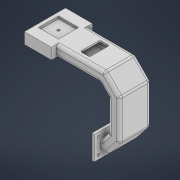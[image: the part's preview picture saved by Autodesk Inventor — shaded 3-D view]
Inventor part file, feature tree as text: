
AUTODESK INVENTOR PART (.ipt)
format: ipt  version: 2021 (Build 250183000, 183)  size: 386,560 bytes
history: native  units: mm
features: sketch x12, fillet x11, extrude x10, sweep x1, shell x1
ambient origin geometry x8: Origin, YZ Plane, XZ Plane, XY Plane, X Axis, Y Axis, Z Axis, Center Point
bodies: Volumenkörper1 (feature_tree)
feature tree (35):
  extrude  "Extrusion1"  Depth=34.2mm
  sweep  "Sweeping1"
  fillet  "Rundung1"  Radius=14.0mm
  fillet  "Rundung2"  Radius=55.9mm
  fillet  "Rundung3"  Radius=90.0mm
  fillet  "Rundung4"  Radius=45.0mm
  fillet  "Rundung5"  Radius=5.0mm
  fillet  "Rundung6"  Radius=58.0mm
  fillet  "Rundung7"  Radius=15.0mm
  fillet  "Rundung8"  [1 undecoded]
  fillet  "Rundung9"  Radius=4.0mm
  shell  "Wandung1"  Thickness=4.0mm
  extrude  "Extrusion2"  Depth=4.0mm
  extrude  "Extrusion3"  Depth=4.0mm
  fillet  "Rundung10"  Radius=4.0mm
  extrude  "Extrusion4"  Depth=4.0mm
  sketch  "Skizze13"  dims[d38=10.0mm d39=0.0mm d40=30.0mm]
  extrude  "Extrusion16"  Depth=2.0mm
  extrude  "Extrusion17"  Depth=10.0mm
  extrude  "Extrusion18"  Depth=2.0mm
  extrude  "Extrusion19"  Depth=2.0mm
  extrude  "Extrusion20"  Depth=5.0mm
  fillet  "Rundung11"  Radius=5.0mm
  extrude  "Extrusion21"  Depth=5.0mm
  sketch  "Skizze1"  dims[d0=52.0mm d1=34.2mm]
  sketch  "Skizze2"  dims[d2=14.0mm d3=0.0mm d4=40.0mm d5=14.0mm d17=55.9mm d18=90.0mm d20=45.0mm d21=5.0mm d22=58.0mm d23=15.0mm d25=0.0mm d26=0.0mm d27=4.0mm d28=4.0mm]
  sketch  "Skizze3"  dims[d29=4.0mm d30=4.0mm]
  sketch  "Skizze4"  dims[d31=4.0mm d32=4.0mm d33=4.0mm]
  sketch  "Skizze5"  dims[d34=4.0mm d35=4.0mm]
  sketch  "Skizze6"  dims[d36=2.0mm d37=2.0mm]
  sketch  "Skizze18"  dims[d41=55.0mm d42=2.0mm]
  sketch  "Skizze20"  dims[d43=3.0mm d44=0.0mm d45=2.0mm]
  sketch  "Skizze21"  dims[d46=3.2mm d47=5.0mm d48=5.0mm]
  sketch  "Skizze22"  dims[d49=3.2mm d50=5.0mm]
  sketch  "Skizze23"  dims[d51=5.0mm d52=3.2mm d53=5.0mm d54=5.0mm d55=3.2mm d56=5.0mm d57=5.0mm d58=3.0mm d59=0.0mm d60=10.0mm d61=36.0mm d62=75.0mm d63=24.668517mm d106=12.0mm d107=25.0mm d108=40.0mm d109=4.5mm d110=0.0mm d111=25.5mm d112=25.5mm d113=12.75mm d114=12.75mm d115=29.0mm d116=29.0mm d117=10.0mm d118=0.0mm d119=3.0mm d120=0.0mm d121=3.2mm d122=3.0mm d123=0.0mm d124=7.0mm d125=8.0mm d126=0.0mm d127=2.0mm d128=2.5mm d129=8.0mm d130=0.0mm]
note: 1 required parameter value undecoded (feature->parameter linkage not recoverable at this tier; creation-order binding heuristic only, values carry confidence <= 0.55)
